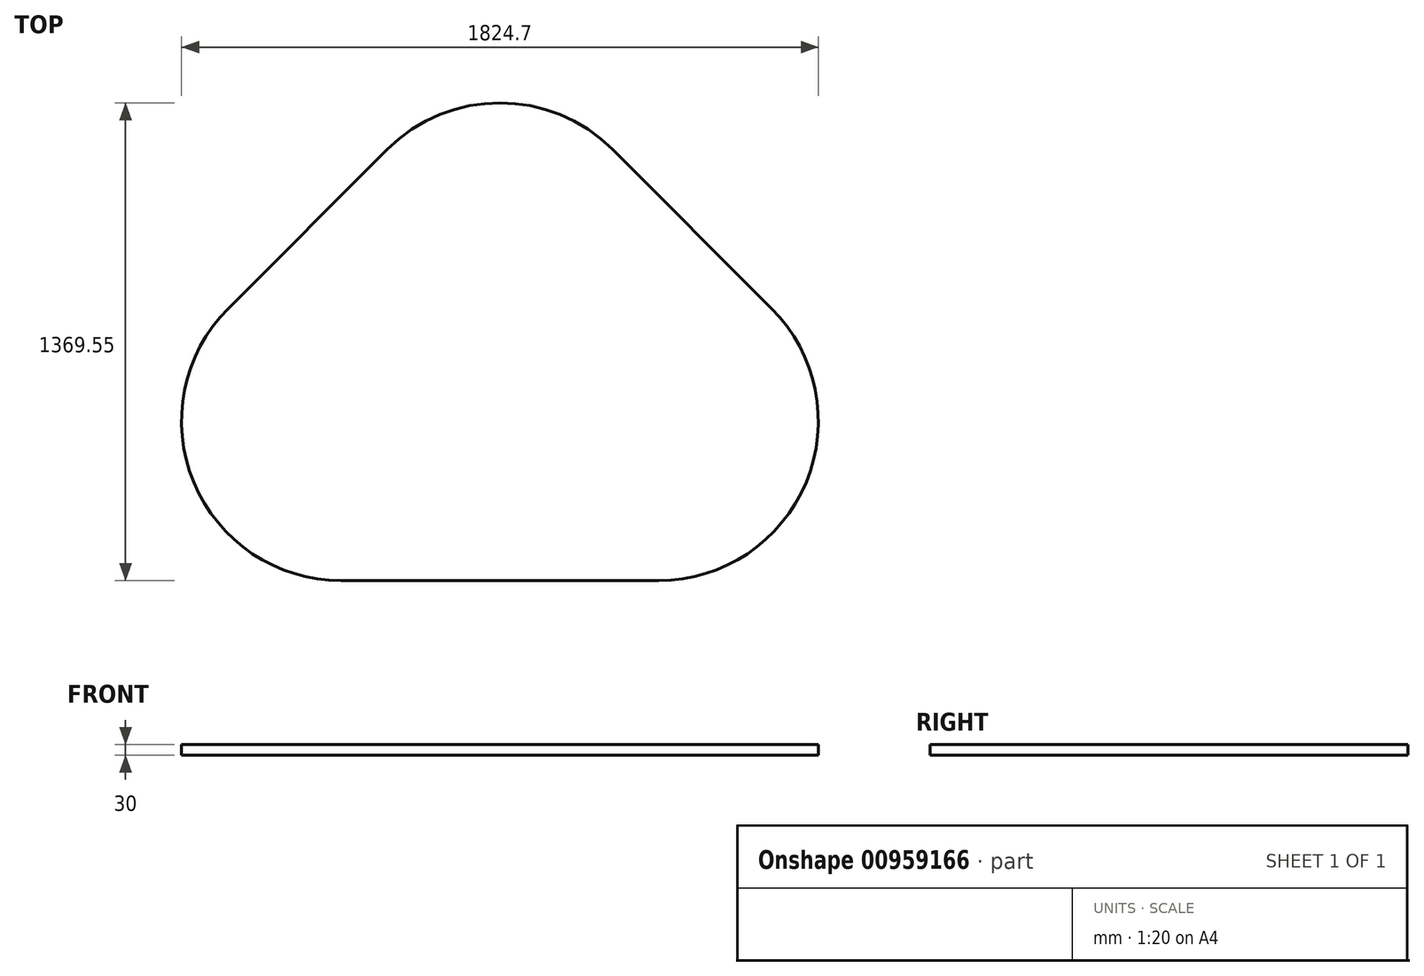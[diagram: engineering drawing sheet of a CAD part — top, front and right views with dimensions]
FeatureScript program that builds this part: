
annotation { "Feature Type Name" : "Feature", "Feature Type Description" : "" }
export const myFeature = defineFeature(function(context is Context, id is Id, definition is map)
    precondition{}
    {
        {
            var Q0;
            Q0=qCreatedBy(makeId("Top.planeOp"),FACE);
            var sketch = newSketch(context, id + "F0", { "sketchPlane" : qUnion([Q0])});
            skLineSegment(sketch, "E0", {"start": v(0, 0) * mm, "end": v(0, 332.68) * mm, "construction": true});
            skLineSegment(sketch, "E1", {"start": v(-455.15, 0) * mm, "end": v(455.15, 0) * mm, "construction": true});
            skLineSegment(sketch, "E2", {"start": v(-1558.93, 0) * mm, "end": v(1558.93, 0) * mm, "construction": true});
            skLineSegment(sketch, "E3", {"start": v(-1558.92, 0) * mm, "end": v(0, 1558.93) * mm, "construction": true});
            skLineSegment(sketch, "E4", {"start": v(0, 332.68) * mm, "end": v(0, 1826.9) * mm, "construction": true});
            skLineSegment(sketch, "E5", {"start": v(0, 1558.93) * mm, "end": v(1558.93, 0) * mm, "construction": true});
            skLineSegment(sketch, "E6", {"start": v(455.15, 457.2) * mm, "end": v(-455.15, 457.2) * mm, "construction": true});
            skLineSegment(sketch, "E7", {"start": v(-455.15, 457.2) * mm, "end": v(0, 912.35) * mm, "construction": true});
            skLineSegment(sketch, "E8", {"start": v(0, 912.35) * mm, "end": v(455.15, 457.2) * mm, "construction": true});
            skArc(sketch, "E9", {"start": v(-43.28, 457.2) * mm, "mid": v(0, 455.15) * mm, "end": v(43.28, 457.2) * mm});
            skArc(sketch, "E10", {"start": v(-778.44, 780.49) * mm, "mid": v(-877.54, 282.24) * mm, "end": v(-455.15, 0) * mm});
            skArc(sketch, "E11.trimOffspring", {"start": v(323.29, 1235.64) * mm, "mid": v(0, 1369.55) * mm, "end": v(-323.29, 1235.64) * mm});
            skArc(sketch, "E12.trimOffspring", {"start": v(455.15, 0) * mm, "mid": v(877.54, 282.24) * mm, "end": v(778.44, 780.49) * mm});
            skLineSegment(sketch, "E13", {"start": v(-323.29, 1235.64) * mm, "end": v(-778.44, 780.49) * mm});
            skLineSegment(sketch, "E14", {"start": v(323.29, 1235.64) * mm, "end": v(778.44, 780.49) * mm});
            skLineSegment(sketch, "E15", {"start": v(455.15, 0) * mm, "end": v(-455.15, 0) * mm});
            skLineSegment(sketch, "E16", {"start": v(-1101.73, 457.2) * mm, "end": v(-644.53, 0) * mm, "construction": true});
            skLineSegment(sketch, "E17", {"start": v(0, 1369.55) * mm, "end": v(-606.02, 1369.55) * mm, "construction": true});
            skSolve(sketch);
        }
        {
            var Q0;
            Q0 = qSketchRegion(id + "F0", true);
            extrude(context, id + "F1", {"entities" : qUnion([Q0]), "depth" : 30 * mm, "offsetDistance" : 25.4 * mm});
        }
    });
